# Revit family: MountingTrack_Soffit_Knotwood
name_source: partatom
category: Specialty Equipment
units: mm (PartAtom-declared; Revit-internal decimal feet)

## family parameters
Classification Number = 23.13.37.23.11
Cut with Voids When Loaded = Yes
Enable Cutting in Views = No
Host = Face
Maintain Annotation Orientation = No
Part Type = Normal
Room Calculation Point = Yes
Round Connector Dimension = Use Diameter
Shared = No

## types (2) — shared parameters
Assembly Code = B3010500
Description = Knotwood Mounted 50mm Mounting Tracks
Export Type to IFC As = ifcBuildingElement
IfcExportAs = ifcBuildingElement
IfcExportType = NOTDEFINED
Manufacturer = Knotwood
ManufacturerSpecCode = KEBCFMT/KEBCSMT
ManufacturerURLProductSpecific = https://www.knotwood.com.au
Model = KEBCFMT/KEBCSMT
ModifiedIssue = 20231214 $
RecommendedSuspensionLength = 1200 mm
Type IFC Predefined Type = NOTDEFINED
URL = https://www.knotwood.com.au
Uniclass2015Code = Pr_20_85_47_50
Uniclass2015Version = Products v1.23
zero-valued in all types: Default Elevation

## per-type parameters (varying)
| type | RailMaterial | TrackMaterial | Uniclass2015Title |
| White | Aluminium_Powdercoat_Knotwood_Textura_White | Aluminium_Powdercoat_Knotwood_Textura_White | Metal hanging rail |
| Black | Aluminium_Powdercoat_Knotwood_Textura_Black | Aluminium_Powdercoat_Knotwood_Textura_Black | Metal hanging rails |

## geometry (parser evidence)
native form markers: Sweep x10
no freeform markers — native parametric forms only
